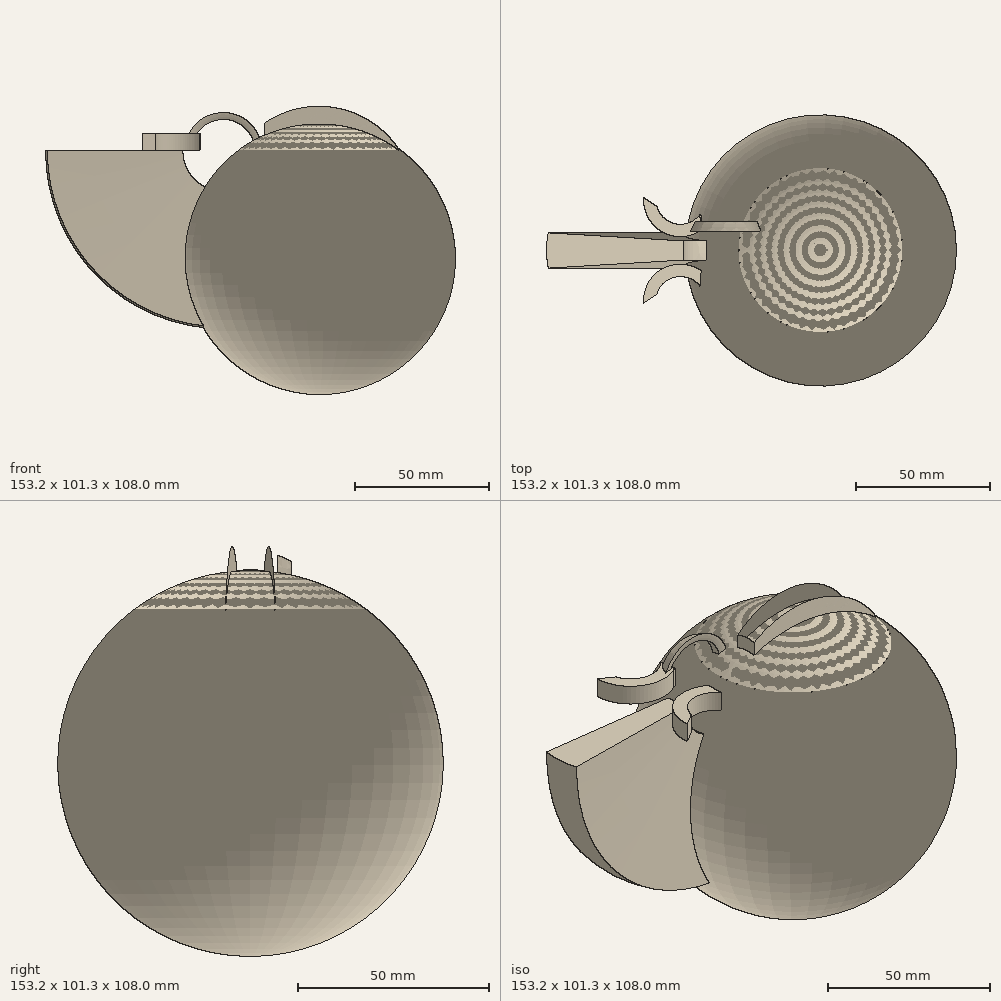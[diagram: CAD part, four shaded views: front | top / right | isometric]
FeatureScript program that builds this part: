
annotation { "Feature Type Name" : "Feature", "Feature Type Description" : "" }
export const myFeature = defineFeature(function(context is Context, id is Id, definition is map)
    precondition{}
    {
        {
            var Q0;
            Q0=qCreatedBy(makeId("Top.planeOp"),FACE);
            var sketch = newSketch(context, id + "F0", { "sketchPlane" : qUnion([Q0])});
            skCircle(sketch, "E0", {"center": v(0, 0) * mm, "radius": 30.57 * mm});
            skLineSegment(sketch, "E1", {"start": v(-51.44, 0) * mm, "end": v(30.57, 0) * mm});
            skEllipse(sketch, "E2", {"center": v(-35.96, 0) * mm, "majorRadius": 15.48 * mm, "minorRadius": 18.58 * mm, "majorAxis": v(1, 0)});
            skPoint(sketch, "E3.orphan", {"position": v(-30.57, 0) * mm});
            skLineSegment(sketch, "E4", {"start": v(-20.77, -3.56) * mm, "end": v(29.85, -6.59) * mm});
            skLineSegment(sketch, "E5.MirrorCS", {"start": v(-20.77, 3.56) * mm, "end": v(29.85, 6.59) * mm});
            skLineSegment(sketch, "E6", {"start": v(-35.96, -18.58) * mm, "end": v(-35.96, 18.58) * mm});
            skArc(sketch, "E7", {"start": v(-64.38, 18.56) * mm, "mid": v(-57.36, 8.07) * mm, "end": v(-44.84, 9.66) * mm});
            skArc(sketch, "E8.MirrorCS", {"start": v(-64.38, -18.56) * mm, "mid": v(-59.91, -9.64) * mm, "end": v(-50.24, -7.18) * mm});
            skPoint(sketch, "E9.orphan", {"position": v(-50.24, 7.18) * mm});
            skArc(sketch, "E10.MirrorCS", {"start": v(-64.38, -18.56) * mm, "mid": v(-58.6, -8.72) * mm, "end": v(-47.2, -8.17) * mm});
            skLineSegment(sketch, "E11.bottom", {"start": v(-48.55, 10.82) * mm, "end": v(-47.65, 10.82) * mm});
            skLineSegment(sketch, "E11.top", {"start": v(-48.55, 4.92) * mm, "end": v(-47.65, 4.92) * mm});
            skLineSegment(sketch, "E11.left", {"start": v(-48.55, 10.82) * mm, "end": v(-48.55, 4.92) * mm});
            skLineSegment(sketch, "E11.right", {"start": v(-47.65, 10.82) * mm, "end": v(-47.65, 4.92) * mm});
            skPoint(sketch, "E12.orphan", {"position": v(-47.2, 8.17) * mm});
            skSolve(sketch);
        }
        {
            var Q0;
            Q0=qCreatedBy(makeId("Front.planeOp"),FACE);
            var sketch = newSketch(context, id + "F1", { "sketchPlane" : qUnion([Q0])});
            skLineSegment(sketch, "E13", {"start": v(0, 0) * mm, "end": v(0, 16.91) * mm});
            skArc(sketch, "E14", {"start": v(30.57, 0) * mm, "mid": v(0, 16.91) * mm, "end": v(-30.57, 0) * mm});
            skLineSegment(sketch, "E15", {"start": v(-30.57, 0) * mm, "end": v(30.57, 0) * mm});
            skArc(sketch, "E16", {"start": v(-20.72, 0) * mm, "mid": v(-36.08, 11.73) * mm, "end": v(-51.45, 0) * mm});
            skLineSegment(sketch, "E17", {"start": v(-51.45, 0) * mm, "end": v(-20.72, 0) * mm});
            skLineSegment(sketch, "E18", {"start": v(-36.08, 0) * mm, "end": v(-36.08, 11.73) * mm});
            skArc(sketch, "E19", {"start": v(30.57, 0) * mm, "mid": v(0, 10.26) * mm, "end": v(-30.57, 0) * mm});
            skSolve(sketch);
        }
        {
            var Q0;
            {var subQ0=sQuery(id+"F1.wireOp",EDGE,"E14");var subQ1=sQuery(id+"F1.wireOp",EDGE,"E13");var subQ2=makeQuery(id+"F1.imprint","INTERSECT",VERTEX,{"derivedFrom":[subQ1,subQ0]});var subQ5=sQuery(id+"F1.wireOp",EDGE,"E15");var subQ8=makeQuery(id+"F1.imprint","INTERSECT",VERTEX,{"derivedFrom":[subQ1,subQ5]});Q0=qUnion([makeQuery(id+"F1.imprint","IMPRINT",FACE,{"disambiguationData":[TD([[makeQuery(id+"F1.imprint","IMPRINT",EDGE,{"disambiguationData":[TD([[subQ8,-1.0]])],"derivedFrom":subQ1}),-1.0]])]}),makeQuery(id+"F1.imprint","IMPRINT",FACE,{"disambiguationData":[TD([[makeQuery(id+"F1.imprint","IMPRINT",EDGE,{"disambiguationData":[TD([[subQ2,1.0]])],"derivedFrom":subQ1}),-1.0]])]})]);}
            var Q1;
            Q1=sQuery(id+"F1.wireOp",EDGE,"E13");
            revolve(context, id + "F2", {"surfaceOperationType" : NewSurfaceOperationType.NEW, "entities" : qUnion([Q0]), "axis" : qUnion([Q1]), "revolveType" : RevolveType.FULL});
        }
        {
            var Q0;
            {var subQ0=sQuery(id+"F0.wireOp",EDGE,"E2");var subQ1=sQuery(id+"F0.wireOp",EDGE,"E1");var subQ2=makeQuery(id+"F0.imprint","INTERSECT",VERTEX,{"disambiguationData":[OD(0.0)],"derivedFrom":[subQ1,subQ0]});Q0=makeQuery(id+"F0.imprint","IMPRINT",FACE,{"disambiguationData":[TD([[makeQuery(id+"F0.imprint","IMPRINT",EDGE,{"disambiguationData":[TD([[subQ2,-1.0]])],"derivedFrom":subQ1}),1.0]])]});}
            var Q1;
            {var subQ0=sQuery(id+"F0.wireOp",EDGE,"E2");var subQ1=sQuery(id+"F0.wireOp",EDGE,"E1");var subQ2=makeQuery(id+"F0.imprint","INTERSECT",VERTEX,{"disambiguationData":[OD(0.0)],"derivedFrom":[subQ1,subQ0]});Q1=makeQuery(id+"F0.imprint","IMPRINT",FACE,{"disambiguationData":[TD([[makeQuery(id+"F0.imprint","IMPRINT",EDGE,{"disambiguationData":[TD([[subQ2,-1.0]])],"derivedFrom":subQ1}),-1.0]])]});}
            var Q2;
            {var subQ5=sQuery(id+"F0.wireOp",EDGE,"E11.bottom");Q2=makeQuery(id+"F0.imprint","IMPRINT",FACE,{"disambiguationData":[TD([[makeQuery(id+"F0.imprint","IMPRINT",EDGE,{"derivedFrom":subQ5}),-1.0]])]});}
            var Q3;
            {var subQ1=sQuery(id+"F0.wireOp",EDGE,"E2");var subQ3=sQuery(id+"F0.wireOp",EDGE,"E7");var subQ4=makeQuery(id+"F0.imprint","INTERSECT",VERTEX,{"derivedFrom":[subQ1,subQ3]});Q3=makeQuery(id+"F0.imprint","IMPRINT",FACE,{"disambiguationData":[TD([[makeQuery(id+"F0.imprint","IMPRINT",EDGE,{"disambiguationData":[TD([[subQ4,-1.0]])],"derivedFrom":subQ3}),1.0]])]});}
            var Q4;
            Q4=sQuery(id+"F0.wireOp",EDGE,"E6");
            revolve(context, id + "F3", {"surfaceOperationType" : NewSurfaceOperationType.NEW, "entities" : qUnion([Q0, Q1, Q2, Q3]), "axis" : qUnion([Q4]), "revolveType" : RevolveType.ONE_DIRECTION, "angle" : 180 * degree});
        }
        {
            var Q0;
            {var subQ3=sQuery(id+"F0.wireOp",EDGE,"E5.MirrorCS");Q0=makeQuery(id+"F0.imprint","IMPRINT",FACE,{"disambiguationData":[TD([[makeQuery(id+"F0.imprint","IMPRINT",EDGE,{"derivedFrom":subQ3}),-1.0]])]});}
            var Q1;
            {var subQ3=sQuery(id+"F0.wireOp",EDGE,"E4");Q1=makeQuery(id+"F0.imprint","IMPRINT",FACE,{"disambiguationData":[TD([[makeQuery(id+"F0.imprint","IMPRINT",EDGE,{"derivedFrom":subQ3}),1.0]])]});}
            extrude(context, id + "F4", {"entities" : qUnion([Q0, Q1]), "operationType" : NewBodyOperationType.REMOVE, "depth" : 25.4 * mm, "offsetDistance" : 25.4 * mm});
        }
        {
            var Q0;
            {var subQ0=sQuery(id+"F1.wireOp",EDGE,"E15");var subQ1=sQuery(id+"F1.wireOp",EDGE,"E13");var subQ2=makeQuery(id+"F1.imprint","INTERSECT",VERTEX,{"derivedFrom":[subQ1,subQ0]});Q0=makeQuery(id+"F1.imprint","IMPRINT",FACE,{"disambiguationData":[TD([[makeQuery(id+"F1.imprint","IMPRINT",EDGE,{"disambiguationData":[TD([[subQ2,-1.0]])],"derivedFrom":subQ1}),-1.0]])]});}
            var Q1;
            Q1=sQuery(id+"F1.wireOp",EDGE,"E13");
            revolve(context, id + "F5", {"surfaceOperationType" : NewSurfaceOperationType.NEW, "entities" : qUnion([Q0]), "axis" : qUnion([Q1]), "revolveType" : RevolveType.FULL});
        }
        {
            var Q0;
            {var subQ5=sQuery(id+"F0.wireOp",EDGE,"E11.top");Q0=makeQuery(id+"F0.imprint","IMPRINT",FACE,{"disambiguationData":[TD([[makeQuery(id+"F0.imprint","IMPRINT",EDGE,{"derivedFrom":subQ5}),1.0]])]});}
            var Q1;
            {var subQ5=sQuery(id+"F0.wireOp",EDGE,"E11.bottom");Q1=makeQuery(id+"F0.imprint","IMPRINT",FACE,{"disambiguationData":[TD([[makeQuery(id+"F0.imprint","IMPRINT",EDGE,{"derivedFrom":subQ5}),-1.0]])]});}
            extrude(context, id + "F6", {"entities" : qUnion([Q0, Q1]), "depth" : 6.35 * mm, "offsetDistance" : 25.4 * mm});
        }
        {
            var Q0;
            Q0=makeQuery(id+"F6.opExtrude","SWEPT_BODY",BODY,{"disambiguationData":[OSD([sQuery(id+"F0.wireOp",EDGE,"E11.bottom"),sQuery(id+"F0.wireOp",EDGE,"E11.top"),sQuery(id+"F0.wireOp",EDGE,"E11.left"),sQuery(id+"F0.wireOp",EDGE,"E11.right")])]});
            transform(context, id + "F7", {"entities" : qUnion([Q0]), "transformType" : TransformType.TRANSLATION_3D, "dx" : 3.1 * mm, "dy" : 2.08 * mm, "dz" : 0 * mm, "makeCopy" : true});
        }
        {
            var Q0;
            Q0=makeQuery(id+"F6.opExtrude","SWEPT_BODY",BODY,{"disambiguationData":[OSD([sQuery(id+"F0.wireOp",EDGE,"E11.bottom"),sQuery(id+"F0.wireOp",EDGE,"E11.top"),sQuery(id+"F0.wireOp",EDGE,"E11.left"),sQuery(id+"F0.wireOp",EDGE,"E11.right")])]});
            deleteBodies(context, id + "F8", {"entities" : qUnion([Q0])});
        }
        {
            var Q0;
            Q0=makeQuery(id+"F7.opPattern","COPY",FACE,{"derivedFrom":makeQuery(id+"F6.opExtrude","SWEPT_FACE",FACE,{"disambiguationData":[OSD([sQuery(id+"F0.wireOp",EDGE,"E11.left")])]}),"instanceName":"1"});
            var Q1;
            Q1=sQuery(id+"F0.wireOp",EDGE,"E7");
            sweep(context, id + "F9", {"profiles" : qUnion([Q0]), "path" : qUnion([Q1])});
        }
        {
            var Q0;
            Q0=makeQuery(id+"F9.opSweep","SWEPT_BODY",BODY,{"disambiguationData":[OSD([sQuery(id+"F0.wireOp",EDGE,"E7"),sQuery(id+"F0.wireOp",EDGE,"E11.left")])]});
            var Q1;
            Q1=qCreatedBy(makeId("Front.planeOp"),FACE);
            mirror(context, id + "F10", {"entities" : qUnion([Q0]), "mirrorPlane" : qUnion([Q1])});
        }
    });
